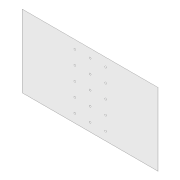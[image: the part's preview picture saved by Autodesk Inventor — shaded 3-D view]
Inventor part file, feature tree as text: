
AUTODESK INVENTOR PART (.ipt)
format: ipt  version: 2012 (Build 160160000, 160)  size: 99,840 bytes
history: native  units: in
note: dims shown in document units (in); Inventor stores cm internally (conversion verified against a paired STEP export)
features: extrude x2, pattern_linear x2, sketch x2
ambient origin geometry x8: Origin, YZ Plane, XZ Plane, XY Plane, X Axis, Y Axis, Z Axis, Center Point
bodies: Solid1 (feature_tree)
feature tree (6):
  extrude  "Extrusion1"  Depth=47.0in
  extrude  "Extrusion2"  Depth=1.125in
  pattern_linear  "Rectangular Pattern1"  Spacing1=8.0in  [1 undecoded]
  pattern_linear  "Rectangular Pattern2"  Spacing1=44.0in  [1 undecoded]
  sketch  "Sketch1"  dims[d0=88.0in d1=47.0in]
  sketch  "Sketch2"  dims[d2=0.125in d3=0.0in d4=1.125in d5=8.0in d6=44.0in d11=5.5in d12=1.9685in d14=9.0in d15=0.3937in d17=1.0in d21=0.125in d22=0.0in d23=0.7874in d25=10.0in d26=0.7874in d28=10.0in]
note: 2 required parameter values undecoded (feature->parameter linkage not recoverable at this tier; creation-order binding heuristic only, values carry confidence <= 0.55)
